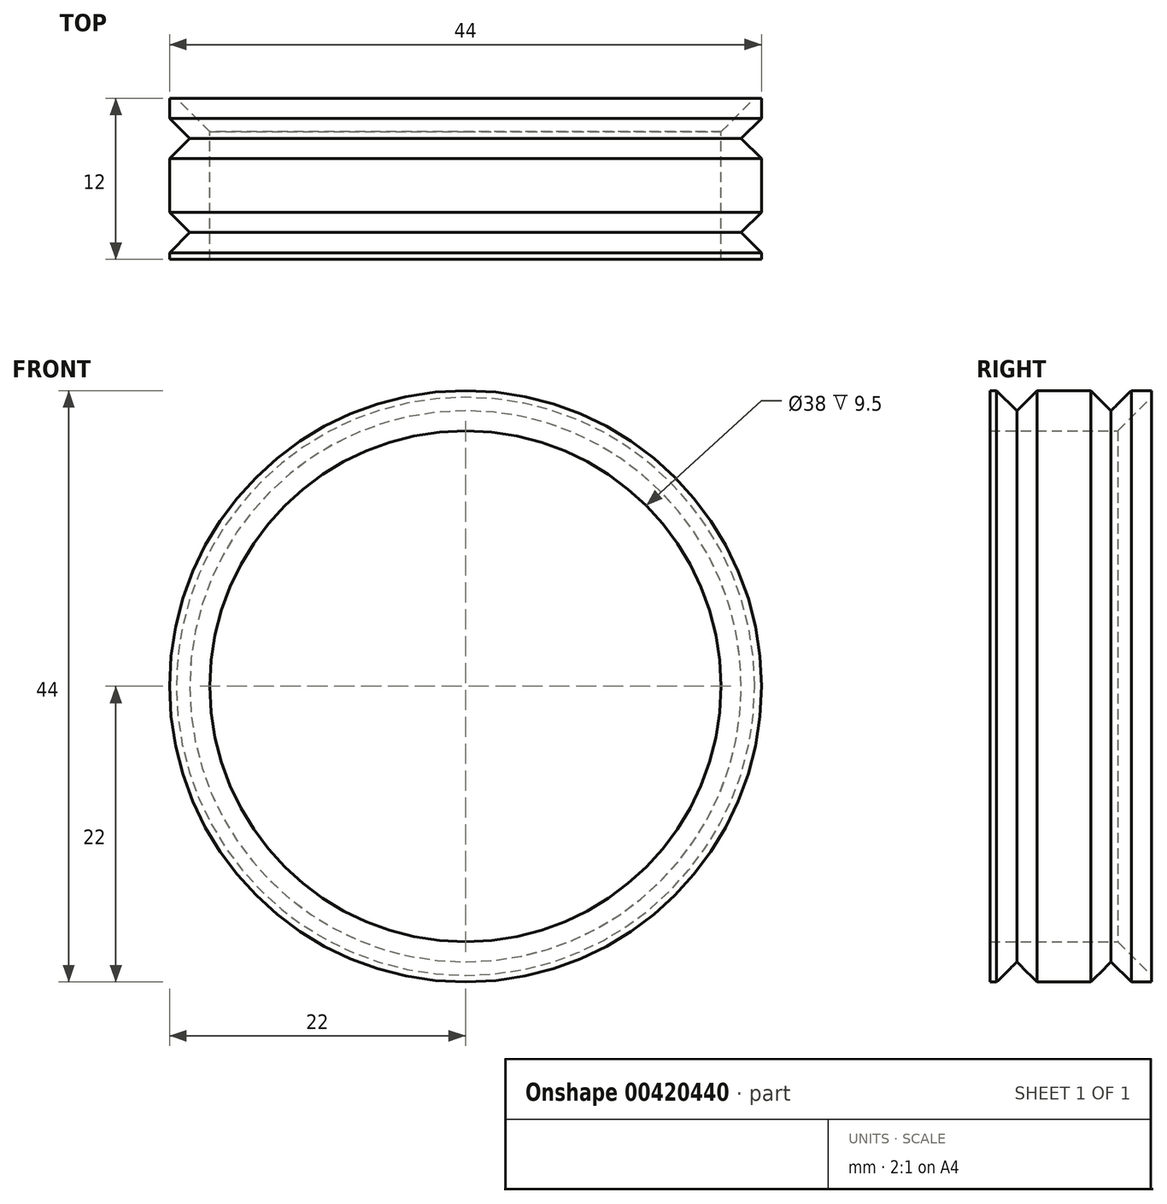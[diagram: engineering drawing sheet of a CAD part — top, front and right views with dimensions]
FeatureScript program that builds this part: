
annotation { "Feature Type Name" : "Feature", "Feature Type Description" : "" }
export const myFeature = defineFeature(function(context is Context, id is Id, definition is map)
    precondition{}
    {
        {
            var Q0;
            Q0=qCreatedBy(makeId("Front.planeOp"),FACE);
            var sketch = newSketch(context, id + "F0", { "sketchPlane" : qUnion([Q0])});
            skCircle(sketch, "E0", {"center": v(0, 0) * mm, "radius": 22 * mm});
            skCircle(sketch, "E1", {"center": v(0, 0) * mm, "radius": 19 * mm});
            skSolve(sketch);
        }
        {
            var Q0;
            Q0 = qSketchRegion(id + "F0", true);
            extrude(context, id + "F1", {"entities" : qUnion([Q0]), "depth" : 7 * mm});
        }
        {
            var Q0;
            Q0=makeQuery(id+"F1.opExtrude","CAP_EDGE",EDGE,{"disambiguationData":[OSD([sQuery(id+"F0.wireOp",EDGE,"E0")])],"isStart":true});
            chamfer(context, id + "F2", {"entities" : qUnion([Q0]), "width" : 1.5 * mm, "tangentPropagation" : true});
        }
        {
            var Q0;
            Q0=makeQuery(id+"F1.opExtrude","CAP_FACE",FACE,{"disambiguationData":[OSD([sQuery(id+"F0.wireOp",EDGE,"E0"),sQuery(id+"F0.wireOp",EDGE,"E1")])],"isStart":true});
            var sketch = newSketch(context, id + "F3", { "sketchPlane" : qUnion([Q0])});
            skCircle(sketch, "E2", {"center": v(0, 0) * mm, "radius": 22 * mm});
            skCircle(sketch, "E3", {"center": v(0, 0) * mm, "radius": 19 * mm});
            skSolve(sketch);
        }
        {
            var Q0;
            Q0 = qSketchRegion(id + "F3", true);
            extrude(context, id + "F4", {"entities" : qUnion([Q0]), "operationType" : NewBodyOperationType.ADD, "depth" : 3 * mm});
        }
        {
            var Q0;
            Q0=makeQuery(id+"F4.opExtrude","CAP_EDGE",EDGE,{"disambiguationData":[OSD([sQuery(id+"F3.wireOp",EDGE,"E2")])],"isStart":true});
            chamfer(context, id + "F5", {"entities" : qUnion([Q0]), "width" : 1.5 * mm, "tangentPropagation" : true});
        }
        {
            var Q0;
            Q0=makeQuery(id+"F4.opExtrude","CAP_EDGE",EDGE,{"disambiguationData":[OSD([sQuery(id+"F3.wireOp",EDGE,"E3")])],"isStart":false});
            chamfer(context, id + "F6", {"entities" : qUnion([Q0]), "width" : 2.5 * mm, "tangentPropagation" : true});
        }
        {
            var Q0;
            Q0=makeQuery(id+"F1.opExtrude","CAP_EDGE",EDGE,{"disambiguationData":[OSD([sQuery(id+"F0.wireOp",EDGE,"E0")])],"isStart":false});
            chamfer(context, id + "F7", {"entities" : qUnion([Q0]), "width" : 1.5 * mm, "tangentPropagation" : true});
        }
        {
            var Q0;
            Q0=makeQuery(id+"F1.opExtrude","CAP_FACE",FACE,{"disambiguationData":[OSD([sQuery(id+"F0.wireOp",EDGE,"E0"),sQuery(id+"F0.wireOp",EDGE,"E1")])],"isStart":false});
            var sketch = newSketch(context, id + "F8", { "sketchPlane" : qUnion([Q0])});
            skCircle(sketch, "E4", {"center": v(0, 0) * mm, "radius": 19 * mm});
            skCircle(sketch, "E5", {"center": v(0, 0) * mm, "radius": 22 * mm});
            skSolve(sketch);
        }
        {
            var Q0;
            Q0 = qSketchRegion(id + "F8", true);
            extrude(context, id + "F9", {"entities" : qUnion([Q0]), "operationType" : NewBodyOperationType.ADD, "depth" : 2 * mm});
        }
        {
            var Q0;
            Q0=makeQuery(id+"F9.opExtrude","CAP_EDGE",EDGE,{"disambiguationData":[OSD([sQuery(id+"F8.wireOp",EDGE,"E5")])],"isStart":true});
            chamfer(context, id + "F10", {"entities" : qUnion([Q0]), "width" : 1.5 * mm, "tangentPropagation" : true});
        }
    });
